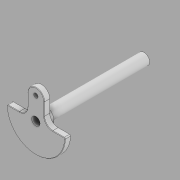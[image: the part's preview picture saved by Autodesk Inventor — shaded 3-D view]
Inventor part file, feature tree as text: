
AUTODESK INVENTOR PART (.ipt)
format: ipt  version: 2020 (Build 240168000, 168)  size: 157,184 bytes
history: native  units: in
note: dims shown in document units (in); Inventor stores cm internally (conversion verified against a paired STEP export)
features: sketch x4, extrude x3, other x1, hole x1, fillet x1
ambient origin geometry x8: Origin, YZ Plane, XZ Plane, XY Plane, X Axis, Y Axis, Z Axis, Center Point
bodies: Body1 (feature_tree)
feature tree (10):
  other  "Sólido1"
  extrude  "Extrusión1"  Depth=0.1875in
  hole  "Agujero1"  [1 undecoded]
  extrude  "Extrusión2"  Depth=0.125in
  extrude  "Extrusión3"  Depth=0.375in
  fillet  "Empalme1"  Radius=0.1875in
  sketch  "Boceto1"  dims[d0=1.3125in d2=0.1875in]
  sketch  "Boceto2"  dims[d3=0.375in d6=0.375in]
  sketch  "Boceto3"  dims[d7=0.125in d8=0.0in d9=0.5in]
  sketch  "Boceto4"  dims[d10=0.0979in d11=0.25in d12=0.119in d13=0.25in d14=0.5635in d15=0.375in d16=0.8108in d17=0.375in d18=0.1875in d19=0.0938in d20=0.0in d21=0.1875in d22=0.0469in d23=0.0469in d24=0.25in d25=2.2188in d26=0.0in d27=0.01in]
note: 1 required parameter value undecoded (feature->parameter linkage not recoverable at this tier; creation-order binding heuristic only, values carry confidence <= 0.55)
